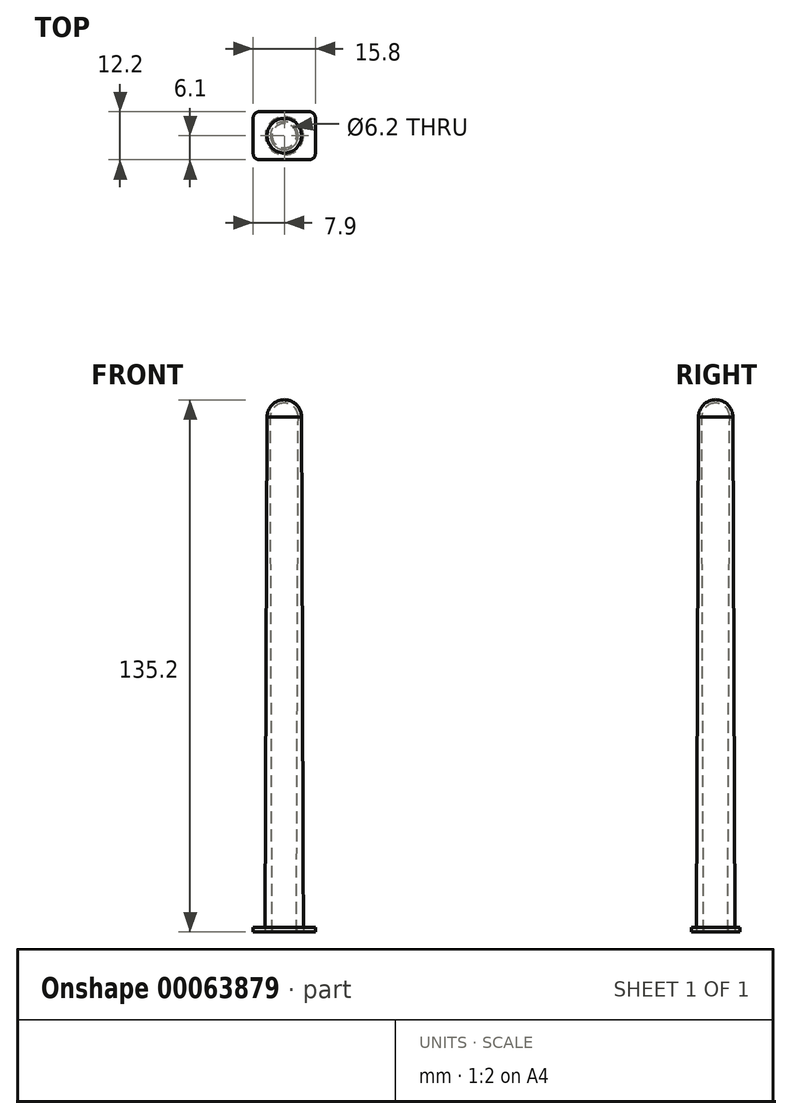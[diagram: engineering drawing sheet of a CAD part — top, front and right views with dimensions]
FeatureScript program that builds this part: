
annotation { "Feature Type Name" : "Feature", "Feature Type Description" : "" }
export const myFeature = defineFeature(function(context is Context, id is Id, definition is map)
    precondition{}
    {
        {
            var Q0;
            Q0=qCreatedBy(makeId("Top.planeOp"),FACE);
            var sketch = newSketch(context, id + "F0", { "sketchPlane" : qUnion([Q0])});
            skLineSegment(sketch, "E0.bottom", {"start": v(0, 0) * mm, "end": v(15.8, 0) * mm});
            skLineSegment(sketch, "E0.top", {"start": v(0, 12.2) * mm, "end": v(15.8, 12.2) * mm});
            skLineSegment(sketch, "E0.left", {"start": v(0, 0) * mm, "end": v(0, 12.2) * mm});
            skLineSegment(sketch, "E0.right", {"start": v(15.8, 0) * mm, "end": v(15.8, 12.2) * mm});
            skCircle(sketch, "E1", {"center": v(7.9, 6.1) * mm, "radius": 3.1 * mm});
            skLineSegment(sketch, "E2", {"start": v(7.9, 6.1) * mm, "end": v(7.9, 12.2) * mm, "construction": true});
            skLineSegment(sketch, "E3", {"start": v(0, 6.1) * mm, "end": v(7.9, 6.1) * mm, "construction": true});
            skSolve(sketch);
        }
        {
            var Q0;
            Q0=makeQuery(id+"F0.imprint","IMPRINT",FACE,{"disambiguationData":[TD([[makeQuery(id+"F0.imprint","IMPRINT",EDGE,{"derivedFrom":sQuery(id+"F0.wireOp",EDGE,"E0.bottom")}),1.0]])]});
            extrude(context, id + "F1", {"entities" : qUnion([Q0]), "depth" : 1.1 * mm});
        }
        {
            var Q0;
            Q0=qCreatedBy(makeId("Top.planeOp"),FACE);
            var sketch = newSketch(context, id + "F2", { "sketchPlane" : qUnion([Q0])});
            skCircle(sketch, "E4", {"center": v(7.9, 6.1) * mm, "radius": 4.85 * mm});
            skCircle(sketch, "E5", {"center": v(7.9, 6.1) * mm, "radius": 3.1 * mm});
            skSolve(sketch);
        }
        {
            var Q0;
            Q0=makeQuery(id+"F2.imprint","IMPRINT",FACE,{"disambiguationData":[TD([[makeQuery(id+"F2.imprint","IMPRINT",EDGE,{"derivedFrom":sQuery(id+"F2.wireOp",EDGE,"E4")}),1.0]])]});
            extrude(context, id + "F3", {"entities" : qUnion([Q0]), "depth" : 130.8 * mm, "hasDraft" : true, "draftAngle" : .2 * degree, "draftPullDirection" : true});
        }
        {
            var Q0;
            Q0=qCreatedBy(makeId("Front.planeOp"),FACE);
            cPlane(context, id + "F4", {"entities" : qUnion([Q0]), "cplaneType" : CPlaneType.OFFSET, "offset" : 6.1 * mm, "oppositeDirection" : true, "width" : 152.4 * mm, "height" : 152.4 * mm});
        }
        {
            var Q0;
            Q0=makeQuery(id+"F3.opExtrude","CAP_FACE",FACE,{"disambiguationData":[OSD([sQuery(id+"F2.wireOp",EDGE,"E4"),sQuery(id+"F2.wireOp",EDGE,"E5")])],"isStart":false});
            var sketch = newSketch(context, id + "F5", { "sketchPlane" : qUnion([Q0])});
            skPoint(sketch, "E6", {"position": v(7.9, 6.1) * mm});
            skSolve(sketch);
        }
        {
            var Q0;
            Q0=qCreatedBy(id+"F4.planeOp",FACE);
            var sketch = newSketch(context, id + "F6", { "sketchPlane" : qUnion([Q0])});
            skArc(sketch, "E7", {"start": v(12.3, 130.8) * mm, "mid": v(11, 133.92) * mm, "end": v(7.9, 135.2) * mm});
            skLineSegment(sketch, "E8", {"start": v(7.9, 135.2) * mm, "end": v(7.9, 130.8) * mm, "construction": true});
            skLineSegment(sketch, "E9", {"start": v(7.9, 130.8) * mm, "end": v(12.3, 130.8) * mm, "construction": true});
            skArc(sketch, "E10", {"start": v(11.46, 130.8) * mm, "mid": v(10.41, 133.32) * mm, "end": v(7.9, 134.37) * mm});
            skLineSegment(sketch, "E11", {"start": v(7.9, 135.2) * mm, "end": v(7.9, 134.37) * mm});
            skLineSegment(sketch, "E12", {"start": v(12.3, 130.8) * mm, "end": v(11.46, 130.8) * mm});
            skSolve(sketch);
        }
        {
            var Q0;
            Q0=makeQuery(id+"F6.imprint","IMPRINT",FACE,{"disambiguationData":[TD([[makeQuery(id+"F6.imprint","IMPRINT",EDGE,{"derivedFrom":sQuery(id+"F6.wireOp",EDGE,"E7")}),1.0]])]});
            var Q1;
            Q1=sQuery(id+"F6.wireOp",EDGE,"E8");
            revolve(context, id + "F7", {"operationType" : NewBodyOperationType.ADD, "entities" : qUnion([Q0]), "axis" : qUnion([Q1]), "revolveType" : RevolveType.FULL});
        }
        {
            var Q0;
            Q0=makeQuery(id+"F1.opExtrude","SWEPT_EDGE",EDGE,{"disambiguationData":[OSD([sQuery(id+"F0.wireOp",EDGE,"E0.bottom"),sQuery(id+"F0.wireOp",EDGE,"E0.right")])]});
            var Q1;
            Q1=makeQuery(id+"F1.opExtrude","SWEPT_EDGE",EDGE,{"disambiguationData":[OSD([sQuery(id+"F0.wireOp",EDGE,"E0.bottom"),sQuery(id+"F0.wireOp",EDGE,"E0.left")])]});
            var Q2;
            Q2=makeQuery(id+"F1.opExtrude","SWEPT_EDGE",EDGE,{"disambiguationData":[OSD([sQuery(id+"F0.wireOp",EDGE,"E0.top"),sQuery(id+"F0.wireOp",EDGE,"E0.right")])]});
            var Q3;
            Q3=makeQuery(id+"F1.opExtrude","SWEPT_EDGE",EDGE,{"disambiguationData":[OSD([sQuery(id+"F0.wireOp",EDGE,"E0.top"),sQuery(id+"F0.wireOp",EDGE,"E0.left")])]});
            fillet(context, id + "F8", {"entities" : qUnion([Q0, Q1, Q2, Q3]), "radius" : 1.59 * mm, "tangentPropagation" : true, "allowEdgeOverflow" : false});
        }
    });
